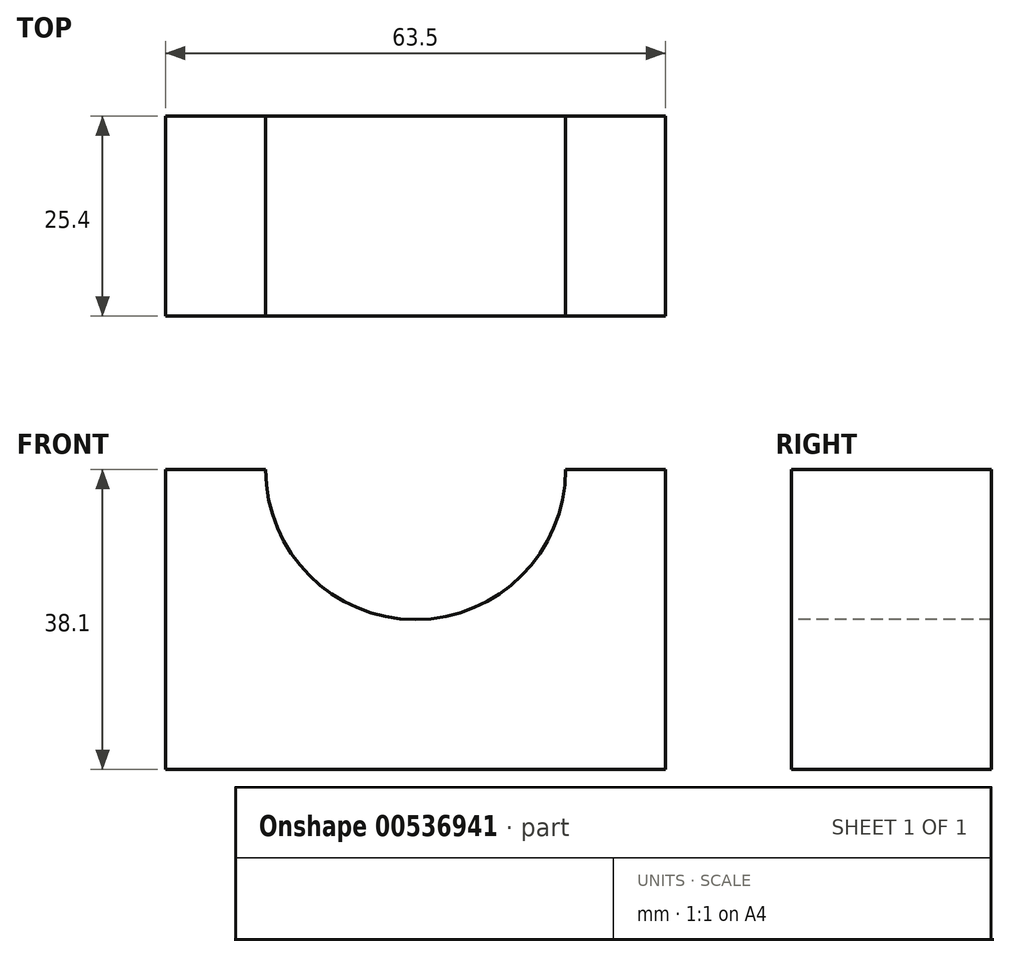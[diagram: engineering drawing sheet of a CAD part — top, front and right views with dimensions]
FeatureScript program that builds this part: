
annotation { "Feature Type Name" : "Feature", "Feature Type Description" : "" }
export const myFeature = defineFeature(function(context is Context, id is Id, definition is map)
    precondition{}
    {
        {
            var Q0;
            Q0=qCreatedBy(makeId("Front.planeOp"),FACE);
            var sketch = newSketch(context, id + "F0", { "sketchPlane" : qUnion([Q0])});
            skLineSegment(sketch, "E0.bottom", {"start": v(-29.62, 0) * mm, "end": v(33.88, 0) * mm});
            skLineSegment(sketch, "E0.top", {"start": v(-29.62, 38.1) * mm, "end": v(33.88, 38.1) * mm});
            skLineSegment(sketch, "E0.left", {"start": v(-29.62, 0) * mm, "end": v(-29.62, 38.1) * mm});
            skLineSegment(sketch, "E0.right", {"start": v(33.88, 0) * mm, "end": v(33.88, 38.1) * mm});
            skSolve(sketch);
        }
        {
            var Q0;
            Q0=makeQuery(id+"F0.imprint","IMPRINT",FACE,{"disambiguationData":[TD([[makeQuery(id+"F0.imprint","IMPRINT",EDGE,{"derivedFrom":sQuery(id+"F0.wireOp",EDGE,"E0.bottom")}),1.0]])]});
            extrude(context, id + "F1", {"entities" : qUnion([Q0]), "depth" : 25.4 * mm, "offsetDistance" : 25.4 * mm});
        }
        {
            var Q0;
            Q0=makeQuery(id+"F1.opExtrude","CAP_FACE",FACE,{"disambiguationData":[OSD([sQuery(id+"F0.wireOp",EDGE,"E0.bottom"),sQuery(id+"F0.wireOp",EDGE,"E0.top"),sQuery(id+"F0.wireOp",EDGE,"E0.left"),sQuery(id+"F0.wireOp",EDGE,"E0.right")])],"isStart":false});
            var sketch = newSketch(context, id + "F2", { "sketchPlane" : qUnion([Q0])});
            skCircle(sketch, "E1", {"center": v(2.13, 38.1) * mm, "radius": 19.05 * mm});
            skSolve(sketch);
        }
        {
            var Q0;
            {var subQ0=sQuery(id+"F2.wireOp",EDGE,"E1");var subQ1=makeQuery(id+"F1.opExtrude","CAP_EDGE",EDGE,{"disambiguationData":[OSD([sQuery(id+"F0.wireOp",EDGE,"E0.top")])],"isStart":false});var subQ2=makeQuery(id+"F2.imprint","INTERSECT",VERTEX,{"disambiguationData":[OD(0.0)],"derivedFrom":[subQ1,subQ0]});Q0=makeQuery(id+"F2.imprint","IMPRINT",FACE,{"disambiguationData":[TD([[makeQuery(id+"F2.imprint","IMPRINT",EDGE,{"disambiguationData":[TD([[subQ2,-1.0]])],"derivedFrom":subQ0}),1.0]])]});}
            extrude(context, id + "F3", {"entities" : qUnion([Q0]), "operationType" : NewBodyOperationType.REMOVE, "oppositeDirection" : true, "depth" : 25.4 * mm, "offsetDistance" : 25.4 * mm});
        }
    });
